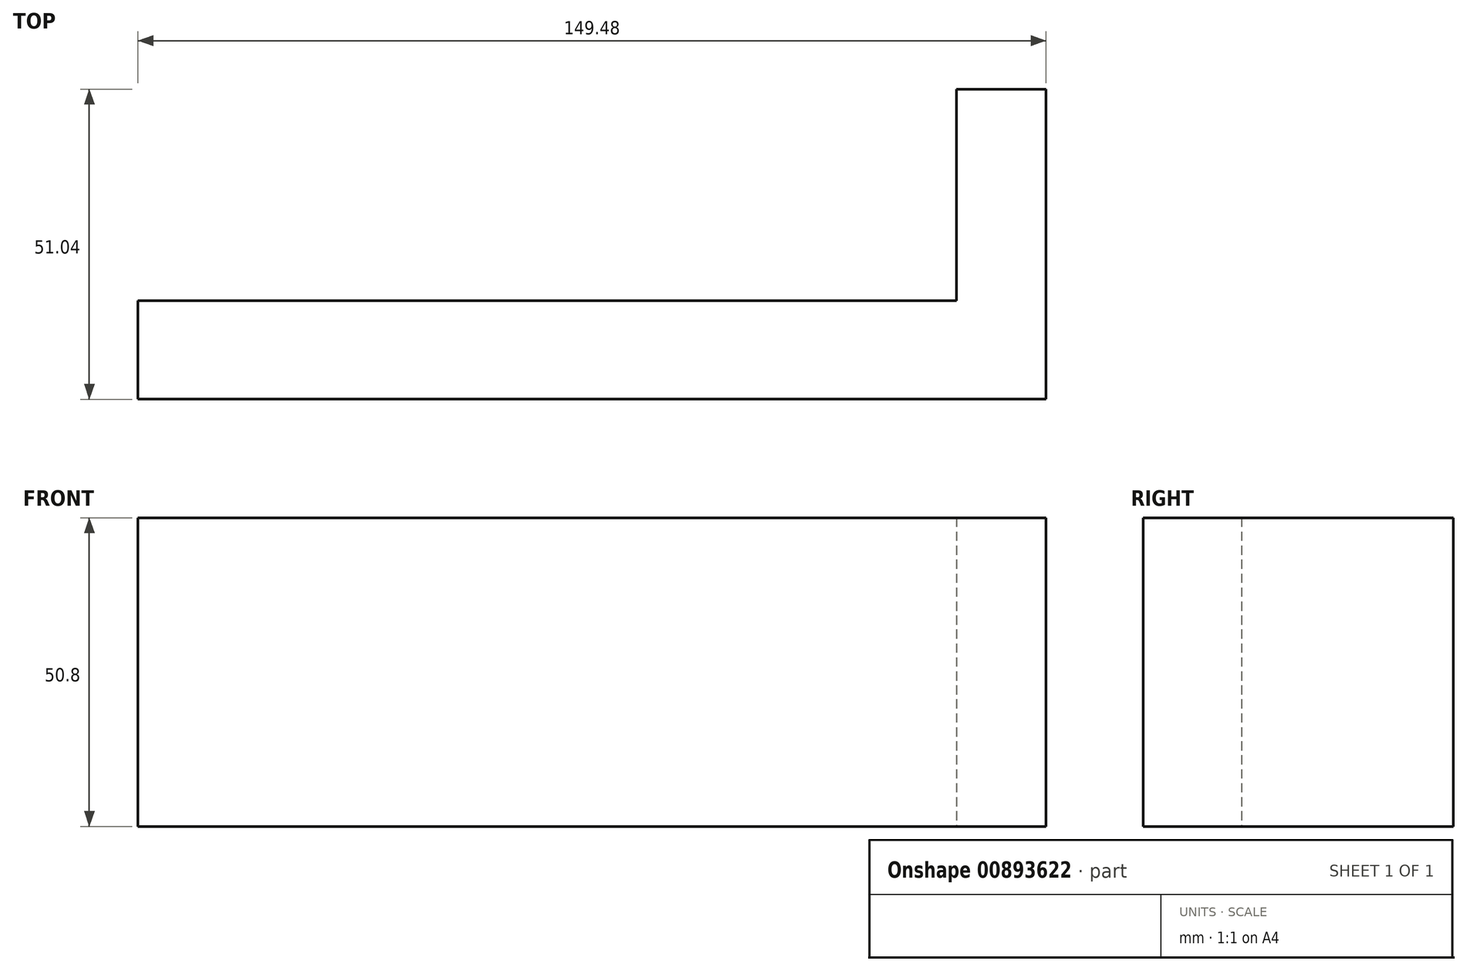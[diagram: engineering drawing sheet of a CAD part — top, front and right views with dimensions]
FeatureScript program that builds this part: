
annotation { "Feature Type Name" : "Feature", "Feature Type Description" : "" }
export const myFeature = defineFeature(function(context is Context, id is Id, definition is map)
    precondition{}
    {
        {
            var Q0;
            Q0=qCreatedBy(makeId("Top.planeOp"),FACE);
            var sketch = newSketch(context, id + "F0", { "sketchPlane" : qUnion([Q0])});
            skLineSegment(sketch, "E0.bottom", {"start": v(74.74, -8.1) * mm, "end": v(-74.74, -8.1) * mm});
            skLineSegment(sketch, "E0.top", {"start": v(74.74, 8.1) * mm, "end": v(-74.74, 8.1) * mm});
            skLineSegment(sketch, "E0.left", {"start": v(74.74, -8.1) * mm, "end": v(74.74, 8.1) * mm});
            skLineSegment(sketch, "E0.right", {"start": v(-74.74, -8.1) * mm, "end": v(-74.74, 8.1) * mm});
            skPoint(sketch, "E0.middle", {"position": v(0, 0) * mm});
            skLineSegment(sketch, "E1", {"start": v(74.74, 8.1) * mm, "end": v(74.74, 42.94) * mm});
            skLineSegment(sketch, "E2", {"start": v(59.97, 42.94) * mm, "end": v(74.74, 42.94) * mm});
            skLineSegment(sketch, "E3", {"start": v(59.97, 42.94) * mm, "end": v(59.97, -8.1) * mm});
            skLineSegment(sketch, "E4", {"start": v(59.97, -8.1) * mm, "end": v(74.74, -8.1) * mm});
            skSolve(sketch);
        }
        {
            var Q0;
            Q0 = qSketchRegion(id + "F0", true);
            extrude(context, id + "F1", {"entities" : qUnion([Q0]), "depth" : 50.8 * mm, "offsetDistance" : 25.4 * mm});
        }
    });
